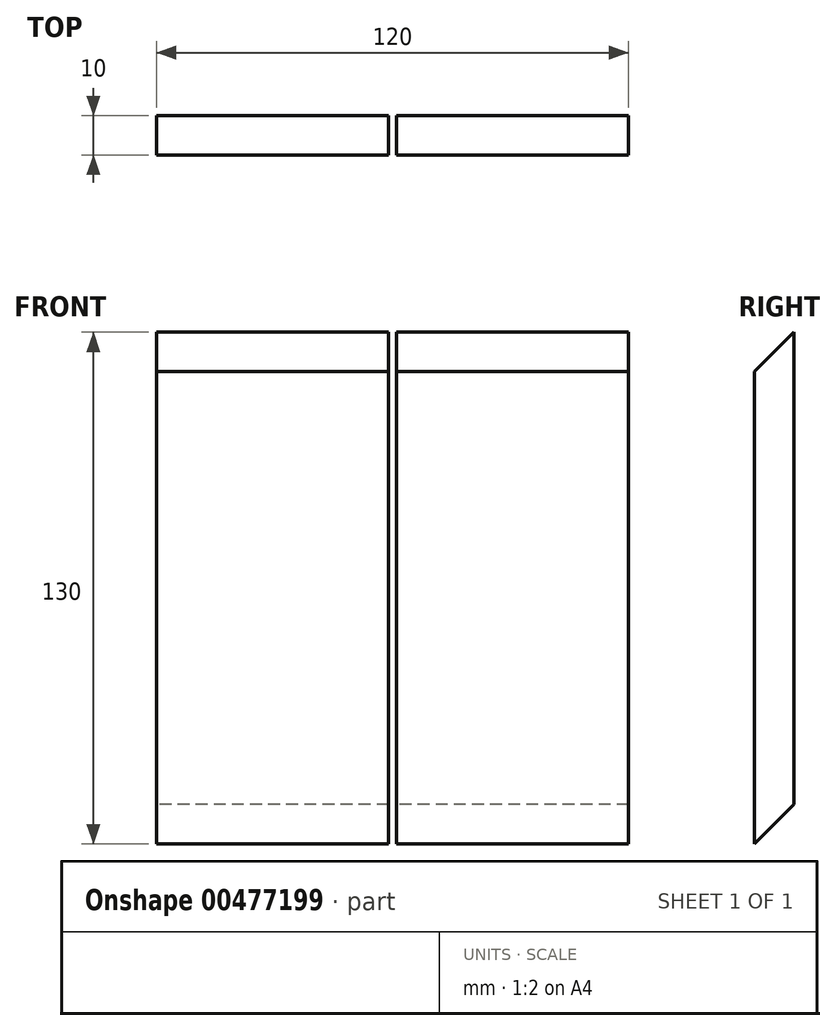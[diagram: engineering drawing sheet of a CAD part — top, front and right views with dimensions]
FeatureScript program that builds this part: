
annotation { "Feature Type Name" : "Feature", "Feature Type Description" : "" }
export const myFeature = defineFeature(function(context is Context, id is Id, definition is map)
    precondition{}
    {
        {
            var Q0;
            Q0=qCreatedBy(makeId("Right.planeOp"),FACE);
            var sketch = newSketch(context, id + "F0", { "sketchPlane" : qUnion([Q0])});
            skLineSegment(sketch, "E0", {"start": v(0, -5) * mm, "end": v(-35, -5) * mm});
            skLineSegment(sketch, "E1", {"start": v(-35, -5) * mm, "end": v(-35, 50) * mm});
            skLineSegment(sketch, "E2", {"start": v(-35, 50) * mm, "end": v(-25, 60) * mm});
            skLineSegment(sketch, "E3", {"start": v(-25, -60) * mm, "end": v(-35, -70) * mm});
            skLineSegment(sketch, "E4", {"start": v(-35, -70) * mm, "end": v(-35, -5) * mm});
            skLineSegment(sketch, "E5", {"start": v(-25, 60) * mm, "end": v(-25, -5) * mm});
            skLineSegment(sketch, "E6", {"start": v(-25, -5) * mm, "end": v(-25, -60) * mm});
            skLineSegment(sketch, "E7", {"start": v(0, 0) * mm, "end": v(0, -5) * mm});
            skSolve(sketch);
        }
        {
            var Q0;
            Q0=qSketchRegion(id+"F0",true);
            extrude(context, id + "F1", {"entities" : qUnion([Q0]), "endBound" : BoundingType.SYMMETRIC, "depth" : 120 * mm});
        }
        {
            var Q0;
            Q0=qCreatedBy(makeId("Right.planeOp"),FACE);
            var sketch = newSketch(context, id + "F2", { "sketchPlane" : qUnion([Q0])});
            skLineSegment(sketch, "E8.bottom", {"start": v(-35, -75) * mm, "end": v(-25, -75) * mm});
            skLineSegment(sketch, "E8.top", {"start": v(-35, 65) * mm, "end": v(-25, 65) * mm});
            skLineSegment(sketch, "E8.left", {"start": v(-35, -75) * mm, "end": v(-35, 65) * mm});
            skLineSegment(sketch, "E8.right", {"start": v(-25, -75) * mm, "end": v(-25, 65) * mm});
            skLineSegment(sketch, "E9", {"start": v(-25, -10) * mm, "end": v(0, -10) * mm});
            skLineSegment(sketch, "E10", {"start": v(0, -10) * mm, "end": v(0, 0) * mm});
            skSolve(sketch);
        }
        {
            var Q0;
            Q0=makeQuery(id+"F2.imprint","IMPRINT",FACE,{"disambiguationData":[TD([[makeQuery(id+"F2.imprint","IMPRINT",EDGE,{"derivedFrom":sQuery(id+"F2.wireOp",EDGE,"E8.bottom")}),1.0]])]});
            extrude(context, id + "F3", {"entities" : qUnion([Q0]), "operationType" : NewBodyOperationType.REMOVE, "endBound" : BoundingType.SYMMETRIC, "oppositeDirection" : true, "depth" : 2 * mm});
        }
    });
